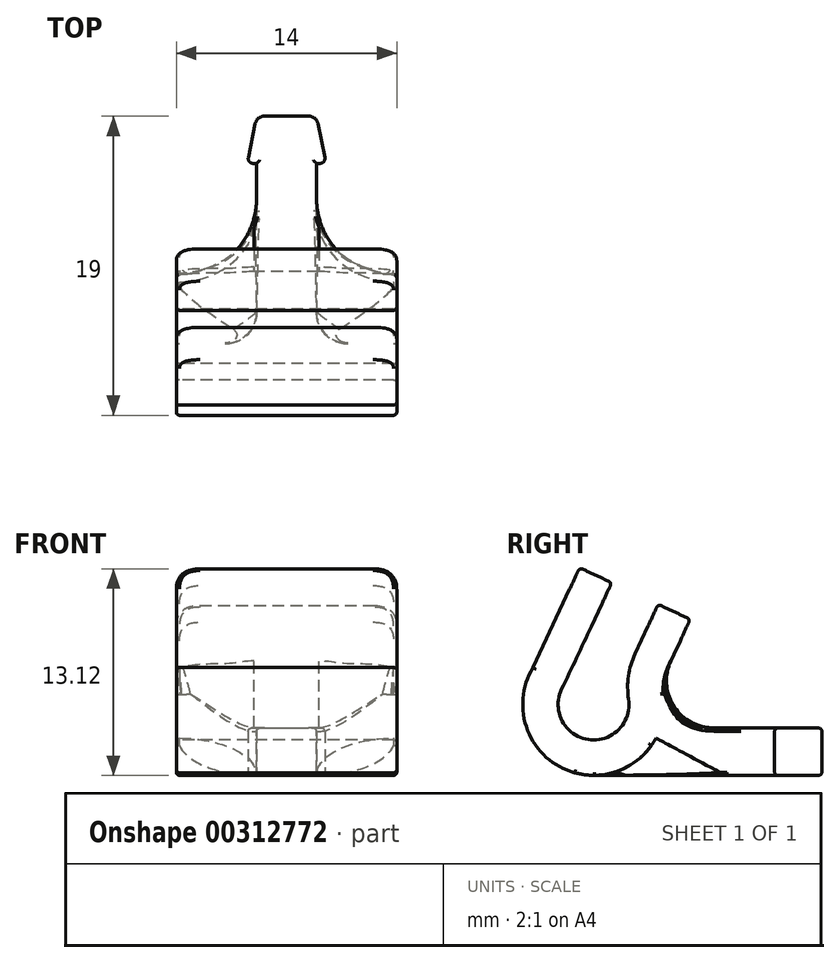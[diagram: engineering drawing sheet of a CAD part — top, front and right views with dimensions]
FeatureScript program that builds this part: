
annotation { "Feature Type Name" : "Feature", "Feature Type Description" : "" }
export const myFeature = defineFeature(function(context is Context, id is Id, definition is map)
    precondition{}
    {
        {
            var Q0;
            Q0=qCreatedBy(makeId("Top.planeOp"),FACE);
            var sketch = newSketch(context, id + "F0", { "sketchPlane" : qUnion([Q0])});
            skLineSegment(sketch, "E0.bottom", {"start": v(-7, -6.95) * mm, "end": v(-3.9, -6.95) * mm});
            skLineSegment(sketch, "E0.top", {"start": v(-7, -8.2) * mm, "end": v(7, -8.2) * mm});
            skLineSegment(sketch, "E0.left", {"start": v(-7, -6.95) * mm, "end": v(-7, -8.2) * mm});
            skLineSegment(sketch, "E0.right", {"start": v(7, -6.95) * mm, "end": v(7, -8.2) * mm});
            skLineSegment(sketch, "E1.bottom", {"start": v(-1.4, 7.5) * mm, "end": v(1.4, 7.5) * mm});
            skLineSegment(sketch, "E1.left", {"start": v(-1.9, 4.5) * mm, "end": v(-1.9, -4.95) * mm});
            skLineSegment(sketch, "E1.right", {"start": v(1.9, 4.5) * mm, "end": v(1.9, -4.95) * mm});
            skLineSegment(sketch, "E2.trimOffspring", {"start": v(3.9, -6.95) * mm, "end": v(7, -6.95) * mm});
            skLineSegment(sketch, "E3", {"start": v(0, 21.87) * mm, "end": v(0, -16.15) * mm, "construction": true});
            skLineSegment(sketch, "E4", {"start": v(-2, 7.02) * mm, "end": v(-2.43, 4.86) * mm});
            skLineSegment(sketch, "E5", {"start": v(-2.13, 4.5) * mm, "end": v(-1.9, 4.5) * mm});
            skLineSegment(sketch, "E6", {"start": v(2.43, 4.86) * mm, "end": v(2, 7.02) * mm});
            skLineSegment(sketch, "E7.trimOffspring", {"start": v(1.9, 4.5) * mm, "end": v(2.13, 4.5) * mm});
            skPoint(sketch, "E8.visualSharp", {"position": v(-1.9, -6.95) * mm});
            skArc(sketch, "E8.filletArc", {"start": v(-3.9, -6.95) * mm, "mid": v(-2.49, -6.36) * mm, "end": v(-1.9, -4.95) * mm});
            skPoint(sketch, "E9.visualSharp", {"position": v(1.9, -6.95) * mm});
            skArc(sketch, "E9.filletArc", {"start": v(1.9, -4.95) * mm, "mid": v(2.49, -6.36) * mm, "end": v(3.9, -6.95) * mm});
            skPoint(sketch, "E10.visualSharp", {"position": v(-1.9, 7.5) * mm});
            skArc(sketch, "E10.filletArc", {"start": v(-1.4, 7.5) * mm, "mid": v(-1.79, 7.36) * mm, "end": v(-2, 7.02) * mm});
            skPoint(sketch, "E11.visualSharp", {"position": v(1.9, 7.5) * mm});
            skArc(sketch, "E11.filletArc", {"start": v(2, 7.02) * mm, "mid": v(1.79, 7.36) * mm, "end": v(1.4, 7.5) * mm});
            skPoint(sketch, "E12.visualSharp", {"position": v(2.5, 4.5) * mm});
            skArc(sketch, "E12.filletArc", {"start": v(2.13, 4.5) * mm, "mid": v(2.37, 4.6) * mm, "end": v(2.43, 4.86) * mm});
            skPoint(sketch, "E13.visualSharp", {"position": v(-2.5, 4.5) * mm});
            skArc(sketch, "E13.filletArc", {"start": v(-2.43, 4.86) * mm, "mid": v(-2.37, 4.6) * mm, "end": v(-2.13, 4.5) * mm});
            skSolve(sketch);
        }
        {
            var Q0;
            Q0 = qSketchRegion(id + "F0", true);
            extrude(context, id + "F1", {"entities" : qUnion([Q0]), "depth" : 3 * mm});
        }
        {
            var Q0;
            Q0=qCreatedBy(makeId("Right.planeOp"),FACE);
            var sketch = newSketch(context, id + "F2", { "sketchPlane" : qUnion([Q0])});
            skArc(sketch, "E14", {"start": v(-10.84, 6.84) * mm, "mid": v(-7.51, 0.03) * mm, "end": v(-2.73, 5.9) * mm});
            skLineSegment(sketch, "E15", {"start": v(-10.84, 6.84) * mm, "end": v(-7.88, 13.19) * mm});
            skLineSegment(sketch, "E16", {"start": v(-7.88, 13.19) * mm, "end": v(-0.86, 9.91) * mm});
            skLineSegment(sketch, "E17", {"start": v(-0.86, 9.91) * mm, "end": v(-2.73, 5.9) * mm});
            skLineSegment(sketch, "E18", {"start": v(-12.4, 0) * mm, "end": v(11.69, 0) * mm, "construction": true});
            skSolve(sketch);
        }
        {
            var Q0;
            Q0 = qSketchRegion(id + "F2", true);
            extrude(context, id + "F3", {"entities" : qUnion([Q0]), "endBound" : BoundingType.SYMMETRIC, "depth" : 14 * mm});
        }
        {
            var Q0;
            Q0=makeQuery(id+"F3.opExtrude","SWEPT_FACE",FACE,{"disambiguationData":[OSD([sQuery(id+"F2.wireOp",EDGE,"E16")])]});
            var Q1;
            Q1=makeQuery(id+"F3.opExtrude","CAP_FACE",FACE,{"disambiguationData":[OSD([sQuery(id+"F2.wireOp",EDGE,"E14"),sQuery(id+"F2.wireOp",EDGE,"E15"),sQuery(id+"F2.wireOp",EDGE,"E16"),sQuery(id+"F2.wireOp",EDGE,"E17")])],"isStart":false});
            var Q2;
            Q2=makeQuery(id+"F3.opExtrude","CAP_FACE",FACE,{"disambiguationData":[OSD([sQuery(id+"F2.wireOp",EDGE,"E14"),sQuery(id+"F2.wireOp",EDGE,"E15"),sQuery(id+"F2.wireOp",EDGE,"E16"),sQuery(id+"F2.wireOp",EDGE,"E17")])],"isStart":true});
            shell(context, id + "F4", {"entities" : qUnion([Q0, Q1, Q2]), "thickness" : 2.25 * mm});
        }
        {
            var Q0;
            Q0=makeQuery(id+"F1.opExtrude","SWEPT_BODY",BODY,{"disambiguationData":[OSD([sQuery(id+"F0.wireOp",EDGE,"E0.bottom"),sQuery(id+"F0.wireOp",EDGE,"E0.top"),sQuery(id+"F0.wireOp",EDGE,"E0.left"),sQuery(id+"F0.wireOp",EDGE,"E0.right"),sQuery(id+"F0.wireOp",EDGE,"E1.bottom"),sQuery(id+"F0.wireOp",EDGE,"E1.left"),sQuery(id+"F0.wireOp",EDGE,"E1.right"),sQuery(id+"F0.wireOp",EDGE,"E2.trimOffspring"),sQuery(id+"F0.wireOp",EDGE,"E4"),sQuery(id+"F0.wireOp",EDGE,"E5"),sQuery(id+"F0.wireOp",EDGE,"E6"),sQuery(id+"F0.wireOp",EDGE,"E7.trimOffspring"),sQuery(id+"F0.wireOp",EDGE,"E8.filletArc"),sQuery(id+"F0.wireOp",EDGE,"E9.filletArc"),sQuery(id+"F0.wireOp",EDGE,"E10.filletArc"),sQuery(id+"F0.wireOp",EDGE,"E11.filletArc"),sQuery(id+"F0.wireOp",EDGE,"E12.filletArc"),sQuery(id+"F0.wireOp",EDGE,"E13.filletArc")])]});
            var Q1;
            Q1=makeQuery(id+"F3.opExtrude","SWEPT_BODY",BODY,{"disambiguationData":[OSD([sQuery(id+"F2.wireOp",EDGE,"E14"),sQuery(id+"F2.wireOp",EDGE,"E15"),sQuery(id+"F2.wireOp",EDGE,"E16"),sQuery(id+"F2.wireOp",EDGE,"E17")])]});
            booleanBodies(context, id + "F5", {"operationType" : BooleanOperationType.UNION, "tools" : qUnion([Q0, Q1])});
        }
        {
            var Q0;
            Q0=makeQuery(id+"F4.opShell","OFFSET_EDGE",EDGE,{"disambiguationData":[OSD([sQuery(id+"F2.wireOp",EDGE,"E14"),sQuery(id+"F2.wireOp",EDGE,"E17")])]});
            fillet(context, id + "F6", {"entities" : qUnion([Q0]), "radius" : 5 * mm, "tangentPropagation" : true, "allowEdgeOverflow" : false});
        }
        {
            var Q0;
            Q0=makeQuery(id+"F5.opBoolean","MERGE",FACE,{"derivedFrom":[makeQuery(id+"F1.opExtrude","SWEPT_FACE",FACE,{"disambiguationData":[OSD([sQuery(id+"F0.wireOp",EDGE,"E0.left")])]}),makeQuery(id+"F3.opExtrude","CAP_FACE",FACE,{"disambiguationData":[OSD([sQuery(id+"F2.wireOp",EDGE,"E14"),sQuery(id+"F2.wireOp",EDGE,"E15"),sQuery(id+"F2.wireOp",EDGE,"E16"),sQuery(id+"F2.wireOp",EDGE,"E17")])],"isStart":true})]});
            var sketch = newSketch(context, id + "F7", { "sketchPlane" : qUnion([Q0])});
            skCircle(sketch, "E19", {"center": v(7, 4.5) * mm, "radius": 2.25 * mm});
            skSolve(sketch);
        }
        {
            var Q0;
            Q0 = qSketchRegion(id + "F7", true);
            extrude(context, id + "F8", {"entities" : qUnion([Q0]), "operationType" : NewBodyOperationType.REMOVE, "endBound" : BoundingType.THROUGH_ALL, "oppositeDirection" : true, "depth" : 14 * mm});
        }
        {
            var Q0;
            Q0=makeQuery(id+"F1.opExtrude","CAP_EDGE",EDGE,{"disambiguationData":[OSD([sQuery(id+"F0.wireOp",EDGE,"E0.top")])],"isStart":true});
            fillet(context, id + "F9", {"entities" : qUnion([Q0]), "radius" : 5 * mm, "tangentPropagation" : true, "allowEdgeOverflow" : false});
        }
        {
            var Q0;
            Q0=makeQuery(id+"F5.opBoolean","INTERSECT",EDGE,{"derivedFrom":[makeQuery(id+"F1.opExtrude","SWEPT_FACE",FACE,{"disambiguationData":[OSD([sQuery(id+"F0.wireOp",EDGE,"E1.right")])]}),makeQuery(id+"F3.opExtrude","SWEPT_FACE",FACE,{"disambiguationData":[OSD([sQuery(id+"F2.wireOp",EDGE,"E14")])]})]});
            var Q1;
            Q1=makeQuery(id+"F5.opBoolean","INTERSECT",EDGE,{"derivedFrom":[makeQuery(id+"F1.opExtrude","SWEPT_FACE",FACE,{"disambiguationData":[OSD([sQuery(id+"F0.wireOp",EDGE,"E9.filletArc")])]}),makeQuery(id+"F3.opExtrude","SWEPT_FACE",FACE,{"disambiguationData":[OSD([sQuery(id+"F2.wireOp",EDGE,"E14")])]})]});
            var Q2;
            {var subQ0=sQuery(id+"F0.wireOp",EDGE,"E1.right");Q2=makeQuery(id+"F11.opFillet","TWEAK_EDGE",EDGE,{"derivedFrom":[makeQuery(id+"F5.opBoolean","INTERSECT",VERTEX,{"derivedFrom":[makeQuery(id+"F1.opExtrude","CAP_FACE",FACE,{"disambiguationData":[OSD([sQuery(id+"F0.wireOp",EDGE,"E0.bottom"),sQuery(id+"F0.wireOp",EDGE,"E0.top"),sQuery(id+"F0.wireOp",EDGE,"E0.left"),sQuery(id+"F0.wireOp",EDGE,"E0.right"),sQuery(id+"F0.wireOp",EDGE,"E1.bottom"),sQuery(id+"F0.wireOp",EDGE,"E1.left"),subQ0,sQuery(id+"F0.wireOp",EDGE,"E2.trimOffspring"),sQuery(id+"F0.wireOp",EDGE,"E4"),sQuery(id+"F0.wireOp",EDGE,"E5"),sQuery(id+"F0.wireOp",EDGE,"E6"),sQuery(id+"F0.wireOp",EDGE,"E7.trimOffspring"),sQuery(id+"F0.wireOp",EDGE,"E8.filletArc"),sQuery(id+"F0.wireOp",EDGE,"E9.filletArc"),sQuery(id+"F0.wireOp",EDGE,"E10.filletArc"),sQuery(id+"F0.wireOp",EDGE,"E11.filletArc"),sQuery(id+"F0.wireOp",EDGE,"E12.filletArc"),sQuery(id+"F0.wireOp",EDGE,"E13.filletArc")])],"isStart":false}),makeQuery(id+"F1.opExtrude","SWEPT_FACE",FACE,{"disambiguationData":[OSD([subQ0])]}),makeQuery(id+"F3.opExtrude","SWEPT_FACE",FACE,{"disambiguationData":[OSD([sQuery(id+"F2.wireOp",EDGE,"E14")])]})]})]});}
            var Q3;
            Q3=makeQuery(id+"F5.opBoolean","INTERSECT",EDGE,{"derivedFrom":[makeQuery(id+"F1.opExtrude","SWEPT_FACE",FACE,{"disambiguationData":[OSD([sQuery(id+"F0.wireOp",EDGE,"E8.filletArc")])]}),makeQuery(id+"F3.opExtrude","SWEPT_FACE",FACE,{"disambiguationData":[OSD([sQuery(id+"F2.wireOp",EDGE,"E14")])]})]});
            var Q4;
            Q4=makeQuery(id+"F5.opBoolean","INTERSECT",EDGE,{"derivedFrom":[makeQuery(id+"F1.opExtrude","SWEPT_FACE",FACE,{"disambiguationData":[OSD([sQuery(id+"F0.wireOp",EDGE,"E1.left")])]}),makeQuery(id+"F3.opExtrude","SWEPT_FACE",FACE,{"disambiguationData":[OSD([sQuery(id+"F2.wireOp",EDGE,"E14")])]})]});
            var Q5;
            {var subQ0=sQuery(id+"F0.wireOp",EDGE,"E1.left");Q5=makeQuery(id+"F11.opFillet","TWEAK_EDGE",EDGE,{"derivedFrom":[makeQuery(id+"F5.opBoolean","INTERSECT",VERTEX,{"derivedFrom":[makeQuery(id+"F1.opExtrude","CAP_FACE",FACE,{"disambiguationData":[OSD([sQuery(id+"F0.wireOp",EDGE,"E0.bottom"),sQuery(id+"F0.wireOp",EDGE,"E0.top"),sQuery(id+"F0.wireOp",EDGE,"E0.left"),sQuery(id+"F0.wireOp",EDGE,"E0.right"),sQuery(id+"F0.wireOp",EDGE,"E1.bottom"),subQ0,sQuery(id+"F0.wireOp",EDGE,"E1.right"),sQuery(id+"F0.wireOp",EDGE,"E2.trimOffspring"),sQuery(id+"F0.wireOp",EDGE,"E4"),sQuery(id+"F0.wireOp",EDGE,"E5"),sQuery(id+"F0.wireOp",EDGE,"E6"),sQuery(id+"F0.wireOp",EDGE,"E7.trimOffspring"),sQuery(id+"F0.wireOp",EDGE,"E8.filletArc"),sQuery(id+"F0.wireOp",EDGE,"E9.filletArc"),sQuery(id+"F0.wireOp",EDGE,"E10.filletArc"),sQuery(id+"F0.wireOp",EDGE,"E11.filletArc"),sQuery(id+"F0.wireOp",EDGE,"E12.filletArc"),sQuery(id+"F0.wireOp",EDGE,"E13.filletArc")])],"isStart":false}),makeQuery(id+"F1.opExtrude","SWEPT_FACE",FACE,{"disambiguationData":[OSD([subQ0])]}),makeQuery(id+"F3.opExtrude","SWEPT_FACE",FACE,{"disambiguationData":[OSD([sQuery(id+"F2.wireOp",EDGE,"E14")])]})]})]});}
            fillet(context, id + "F10", {"entities" : qUnion([Q0, Q1, Q2, Q3, Q4, Q5]), "radius" : 5 * mm, "tangentPropagation" : true, "allowEdgeOverflow" : false});
        }
        {
            var Q0;
            Q0=makeQuery(id+"F5.opBoolean","INTERSECT",EDGE,{"derivedFrom":[makeQuery(id+"F1.opExtrude","CAP_FACE",FACE,{"disambiguationData":[OSD([sQuery(id+"F0.wireOp",EDGE,"E0.bottom"),sQuery(id+"F0.wireOp",EDGE,"E0.top"),sQuery(id+"F0.wireOp",EDGE,"E0.left"),sQuery(id+"F0.wireOp",EDGE,"E0.right"),sQuery(id+"F0.wireOp",EDGE,"E1.bottom"),sQuery(id+"F0.wireOp",EDGE,"E1.left"),sQuery(id+"F0.wireOp",EDGE,"E1.right"),sQuery(id+"F0.wireOp",EDGE,"E2.trimOffspring"),sQuery(id+"F0.wireOp",EDGE,"E4"),sQuery(id+"F0.wireOp",EDGE,"E5"),sQuery(id+"F0.wireOp",EDGE,"E6"),sQuery(id+"F0.wireOp",EDGE,"E7.trimOffspring"),sQuery(id+"F0.wireOp",EDGE,"E8.filletArc"),sQuery(id+"F0.wireOp",EDGE,"E9.filletArc"),sQuery(id+"F0.wireOp",EDGE,"E10.filletArc"),sQuery(id+"F0.wireOp",EDGE,"E11.filletArc"),sQuery(id+"F0.wireOp",EDGE,"E12.filletArc"),sQuery(id+"F0.wireOp",EDGE,"E13.filletArc")])],"isStart":false}),makeQuery(id+"F3.opExtrude","SWEPT_FACE",FACE,{"disambiguationData":[OSD([sQuery(id+"F2.wireOp",EDGE,"E14")])]})]});
            fillet(context, id + "F11", {"entities" : qUnion([Q0]), "radius" : 4 * mm, "tangentPropagation" : true, "rho" : 0.6, "crossSection" : FilletCrossSection.CONIC, "allowEdgeOverflow" : false});
        }
        {
            var Q0;
            Q0=makeQuery(id+"F3.opExtrude","CAP_EDGE",EDGE,{"disambiguationData":[OSD([sQuery(id+"F2.wireOp",EDGE,"E16")])],"isStart":true});
            var Q1;
            {var subQ0=sQuery(id+"F2.wireOp",EDGE,"E16");Q1=makeQuery(id+"F4.opShell","OFFSET_EDGE",EDGE,{"disambiguationData":[OSD([subQ0]),TDD([makeQuery(id+"F3.opExtrude","CAP_EDGE",EDGE,{"disambiguationData":[OSD([subQ0])],"isStart":true})])]});}
            var Q2;
            Q2=makeQuery(id+"F3.opExtrude","CAP_EDGE",EDGE,{"disambiguationData":[OSD([sQuery(id+"F2.wireOp",EDGE,"E16")])],"isStart":false});
            var Q3;
            {var subQ0=sQuery(id+"F2.wireOp",EDGE,"E16");Q3=makeQuery(id+"F4.opShell","OFFSET_EDGE",EDGE,{"disambiguationData":[OSD([subQ0]),TDD([makeQuery(id+"F3.opExtrude","CAP_EDGE",EDGE,{"disambiguationData":[OSD([subQ0])],"isStart":false})])]});}
            fillet(context, id + "F12", {"entities" : qUnion([Q0, Q1, Q2, Q3]), "radius" : 1.5 * mm, "tangentPropagation" : true, "rho" : 0.5, "crossSection" : FilletCrossSection.CONIC, "allowEdgeOverflow" : false});
        }
        {
            var Q0;
            {var subQ0=sQuery(id+"F0.wireOp",EDGE,"E8.filletArc");var subQ1=sQuery(id+"F0.wireOp",EDGE,"E2.trimOffspring");var subQ3=sQuery(id+"F0.wireOp",EDGE,"E1.right");var subQ4=sQuery(id+"F0.wireOp",EDGE,"E1.left");var subQ5=sQuery(id+"F0.wireOp",EDGE,"E0.bottom");var subQ6=sQuery(id+"F0.wireOp",EDGE,"E0.right");var subQ9=sQuery(id+"F2.wireOp",EDGE,"E14");var subQ10=sQuery(id+"F0.wireOp",EDGE,"E9.filletArc");var subQ11=sQuery(id+"F0.wireOp",EDGE,"E0.left");var subQ12=makeQuery(id+"F1.opExtrude","CAP_FACE",FACE,{"disambiguationData":[OSD([subQ5,sQuery(id+"F0.wireOp",EDGE,"E0.top"),subQ11,subQ6,sQuery(id+"F0.wireOp",EDGE,"E1.bottom"),subQ4,subQ3,subQ1,sQuery(id+"F0.wireOp",EDGE,"E4"),sQuery(id+"F0.wireOp",EDGE,"E5"),sQuery(id+"F0.wireOp",EDGE,"E6"),sQuery(id+"F0.wireOp",EDGE,"E7.trimOffspring"),subQ0,subQ10,sQuery(id+"F0.wireOp",EDGE,"E10.filletArc"),sQuery(id+"F0.wireOp",EDGE,"E11.filletArc"),sQuery(id+"F0.wireOp",EDGE,"E12.filletArc"),sQuery(id+"F0.wireOp",EDGE,"E13.filletArc")])],"isStart":false});var subQ13=makeQuery(id+"F3.opExtrude","SWEPT_FACE",FACE,{"disambiguationData":[OSD([subQ9])]});Q0=makeQuery(id+"F11.opFillet","BLEND_EDGE",EDGE,{"blendedFrom":[makeQuery(id+"F5.opBoolean","INTERSECT",EDGE,{"derivedFrom":[subQ12,subQ13]}),makeQuery(id+"F5.opBoolean","SPLIT",FACE,{"disambiguationData":[TD([makeQuery(id+"F1.opExtrude","SWEPT_FACE",FACE,{"disambiguationData":[OSD([subQ5])]})])],"derivedFrom":subQ13})],"blendedInto":[makeQuery(id+"F5.opBoolean","SPLIT",FACE,{"disambiguationData":[TD([makeQuery(id+"F1.opExtrude","SWEPT_FACE",FACE,{"disambiguationData":[OSD([subQ5])]})])],"derivedFrom":subQ13})]});}
            var Q1;
            Q1=makeQuery(id+"F3.opExtrude","SWEPT_EDGE",EDGE,{"disambiguationData":[OSD([sQuery(id+"F2.wireOp",EDGE,"E14"),sQuery(id+"F2.wireOp",EDGE,"E17")])]});
            fillet(context, id + "F13", {"entities" : qUnion([Q0, Q1]), "radius" : 3 * mm, "tangentPropagation" : true, "allowEdgeOverflow" : false});
        }
        {
            var Q0;
            Q0=makeQuery(id+"F1.opExtrude","CAP_EDGE",EDGE,{"disambiguationData":[OSD([sQuery(id+"F0.wireOp",EDGE,"E1.bottom")])],"isStart":true});
            var Q1;
            Q1=makeQuery(id+"F1.opExtrude","CAP_EDGE",EDGE,{"disambiguationData":[OSD([sQuery(id+"F0.wireOp",EDGE,"E11.filletArc")])],"isStart":true});
            var Q2;
            Q2=makeQuery(id+"F1.opExtrude","CAP_EDGE",EDGE,{"disambiguationData":[OSD([sQuery(id+"F0.wireOp",EDGE,"E6")])],"isStart":true});
            var Q3;
            Q3=makeQuery(id+"F1.opExtrude","CAP_EDGE",EDGE,{"disambiguationData":[OSD([sQuery(id+"F0.wireOp",EDGE,"E12.filletArc")])],"isStart":true});
            var Q4;
            Q4=makeQuery(id+"F1.opExtrude","CAP_EDGE",EDGE,{"disambiguationData":[OSD([sQuery(id+"F0.wireOp",EDGE,"E7.trimOffspring")])],"isStart":true});
            var Q5;
            Q5=makeQuery(id+"F1.opExtrude","CAP_EDGE",EDGE,{"disambiguationData":[OSD([sQuery(id+"F0.wireOp",EDGE,"E1.right")])],"isStart":true});
            var Q6;
            Q6=makeQuery(id+"F1.opExtrude","CAP_EDGE",EDGE,{"disambiguationData":[OSD([sQuery(id+"F0.wireOp",EDGE,"E10.filletArc")])],"isStart":true});
            var Q7;
            Q7=makeQuery(id+"F1.opExtrude","CAP_EDGE",EDGE,{"disambiguationData":[OSD([sQuery(id+"F0.wireOp",EDGE,"E4")])],"isStart":true});
            var Q8;
            Q8=makeQuery(id+"F1.opExtrude","CAP_EDGE",EDGE,{"disambiguationData":[OSD([sQuery(id+"F0.wireOp",EDGE,"E13.filletArc")])],"isStart":true});
            var Q9;
            Q9=makeQuery(id+"F1.opExtrude","CAP_EDGE",EDGE,{"disambiguationData":[OSD([sQuery(id+"F0.wireOp",EDGE,"E5")])],"isStart":true});
            var Q10;
            Q10=makeQuery(id+"F1.opExtrude","CAP_EDGE",EDGE,{"disambiguationData":[OSD([sQuery(id+"F0.wireOp",EDGE,"E1.left")])],"isStart":true});
            var Q11;
            {var subQ0=sQuery(id+"F0.wireOp",EDGE,"E1.left");Q11=makeQuery(id+"F10.opFillet","BLEND_EDGE",EDGE,{"blendedFrom":[makeQuery(id+"F5.opBoolean","INTERSECT",EDGE,{"derivedFrom":[makeQuery(id+"F1.opExtrude","SWEPT_FACE",FACE,{"disambiguationData":[OSD([subQ0])]}),makeQuery(id+"F3.opExtrude","SWEPT_FACE",FACE,{"disambiguationData":[OSD([sQuery(id+"F2.wireOp",EDGE,"E14")])]})]}),makeQuery(id+"F1.opExtrude","CAP_FACE",FACE,{"disambiguationData":[OSD([sQuery(id+"F0.wireOp",EDGE,"E0.bottom"),sQuery(id+"F0.wireOp",EDGE,"E0.top"),sQuery(id+"F0.wireOp",EDGE,"E0.left"),sQuery(id+"F0.wireOp",EDGE,"E0.right"),sQuery(id+"F0.wireOp",EDGE,"E1.bottom"),subQ0,sQuery(id+"F0.wireOp",EDGE,"E1.right"),sQuery(id+"F0.wireOp",EDGE,"E2.trimOffspring"),sQuery(id+"F0.wireOp",EDGE,"E4"),sQuery(id+"F0.wireOp",EDGE,"E5"),sQuery(id+"F0.wireOp",EDGE,"E6"),sQuery(id+"F0.wireOp",EDGE,"E7.trimOffspring"),sQuery(id+"F0.wireOp",EDGE,"E8.filletArc"),sQuery(id+"F0.wireOp",EDGE,"E9.filletArc"),sQuery(id+"F0.wireOp",EDGE,"E10.filletArc"),sQuery(id+"F0.wireOp",EDGE,"E11.filletArc"),sQuery(id+"F0.wireOp",EDGE,"E12.filletArc"),sQuery(id+"F0.wireOp",EDGE,"E13.filletArc")])],"isStart":true})],"blendedInto":[makeQuery(id+"F1.opExtrude","CAP_FACE",FACE,{"disambiguationData":[OSD([sQuery(id+"F0.wireOp",EDGE,"E0.bottom"),sQuery(id+"F0.wireOp",EDGE,"E0.top"),sQuery(id+"F0.wireOp",EDGE,"E0.left"),sQuery(id+"F0.wireOp",EDGE,"E0.right"),sQuery(id+"F0.wireOp",EDGE,"E1.bottom"),subQ0,sQuery(id+"F0.wireOp",EDGE,"E1.right"),sQuery(id+"F0.wireOp",EDGE,"E2.trimOffspring"),sQuery(id+"F0.wireOp",EDGE,"E4"),sQuery(id+"F0.wireOp",EDGE,"E5"),sQuery(id+"F0.wireOp",EDGE,"E6"),sQuery(id+"F0.wireOp",EDGE,"E7.trimOffspring"),sQuery(id+"F0.wireOp",EDGE,"E8.filletArc"),sQuery(id+"F0.wireOp",EDGE,"E9.filletArc"),sQuery(id+"F0.wireOp",EDGE,"E10.filletArc"),sQuery(id+"F0.wireOp",EDGE,"E11.filletArc"),sQuery(id+"F0.wireOp",EDGE,"E12.filletArc"),sQuery(id+"F0.wireOp",EDGE,"E13.filletArc")])],"isStart":true})]});}
            var Q12;
            {var subQ0=sQuery(id+"F0.wireOp",EDGE,"E1.right");Q12=makeQuery(id+"F10.opFillet","BLEND_EDGE",EDGE,{"blendedFrom":[makeQuery(id+"F5.opBoolean","INTERSECT",EDGE,{"derivedFrom":[makeQuery(id+"F1.opExtrude","SWEPT_FACE",FACE,{"disambiguationData":[OSD([subQ0])]}),makeQuery(id+"F3.opExtrude","SWEPT_FACE",FACE,{"disambiguationData":[OSD([sQuery(id+"F2.wireOp",EDGE,"E14")])]})]}),makeQuery(id+"F1.opExtrude","CAP_FACE",FACE,{"disambiguationData":[OSD([sQuery(id+"F0.wireOp",EDGE,"E0.bottom"),sQuery(id+"F0.wireOp",EDGE,"E0.top"),sQuery(id+"F0.wireOp",EDGE,"E0.left"),sQuery(id+"F0.wireOp",EDGE,"E0.right"),sQuery(id+"F0.wireOp",EDGE,"E1.bottom"),sQuery(id+"F0.wireOp",EDGE,"E1.left"),subQ0,sQuery(id+"F0.wireOp",EDGE,"E2.trimOffspring"),sQuery(id+"F0.wireOp",EDGE,"E4"),sQuery(id+"F0.wireOp",EDGE,"E5"),sQuery(id+"F0.wireOp",EDGE,"E6"),sQuery(id+"F0.wireOp",EDGE,"E7.trimOffspring"),sQuery(id+"F0.wireOp",EDGE,"E8.filletArc"),sQuery(id+"F0.wireOp",EDGE,"E9.filletArc"),sQuery(id+"F0.wireOp",EDGE,"E10.filletArc"),sQuery(id+"F0.wireOp",EDGE,"E11.filletArc"),sQuery(id+"F0.wireOp",EDGE,"E12.filletArc"),sQuery(id+"F0.wireOp",EDGE,"E13.filletArc")])],"isStart":true})],"blendedInto":[makeQuery(id+"F1.opExtrude","CAP_FACE",FACE,{"disambiguationData":[OSD([sQuery(id+"F0.wireOp",EDGE,"E0.bottom"),sQuery(id+"F0.wireOp",EDGE,"E0.top"),sQuery(id+"F0.wireOp",EDGE,"E0.left"),sQuery(id+"F0.wireOp",EDGE,"E0.right"),sQuery(id+"F0.wireOp",EDGE,"E1.bottom"),sQuery(id+"F0.wireOp",EDGE,"E1.left"),subQ0,sQuery(id+"F0.wireOp",EDGE,"E2.trimOffspring"),sQuery(id+"F0.wireOp",EDGE,"E4"),sQuery(id+"F0.wireOp",EDGE,"E5"),sQuery(id+"F0.wireOp",EDGE,"E6"),sQuery(id+"F0.wireOp",EDGE,"E7.trimOffspring"),sQuery(id+"F0.wireOp",EDGE,"E8.filletArc"),sQuery(id+"F0.wireOp",EDGE,"E9.filletArc"),sQuery(id+"F0.wireOp",EDGE,"E10.filletArc"),sQuery(id+"F0.wireOp",EDGE,"E11.filletArc"),sQuery(id+"F0.wireOp",EDGE,"E12.filletArc"),sQuery(id+"F0.wireOp",EDGE,"E13.filletArc")])],"isStart":true})]});}
            fillet(context, id + "F14", {"entities" : qUnion([Q0, Q1, Q2, Q3, Q4, Q5, Q6, Q7, Q8, Q9, Q10, Q11, Q12]), "radius" : 0.2 * mm, "tangentPropagation" : true, "allowEdgeOverflow" : false});
        }
        {
            var Q0;
            {var subQ0=sQuery(id+"F2.wireOp",EDGE,"E14");var subQ1=sQuery(id+"F0.wireOp",EDGE,"E1.left");Q0=makeQuery(id+"F11.opFillet","BLEND_EDGE",EDGE,{"blendedFrom":[makeQuery(id+"F5.opBoolean","INTERSECT",EDGE,{"derivedFrom":[makeQuery(id+"F1.opExtrude","CAP_FACE",FACE,{"disambiguationData":[OSD([sQuery(id+"F0.wireOp",EDGE,"E0.bottom"),sQuery(id+"F0.wireOp",EDGE,"E0.top"),sQuery(id+"F0.wireOp",EDGE,"E0.left"),sQuery(id+"F0.wireOp",EDGE,"E0.right"),sQuery(id+"F0.wireOp",EDGE,"E1.bottom"),subQ1,sQuery(id+"F0.wireOp",EDGE,"E1.right"),sQuery(id+"F0.wireOp",EDGE,"E2.trimOffspring"),sQuery(id+"F0.wireOp",EDGE,"E4"),sQuery(id+"F0.wireOp",EDGE,"E5"),sQuery(id+"F0.wireOp",EDGE,"E6"),sQuery(id+"F0.wireOp",EDGE,"E7.trimOffspring"),sQuery(id+"F0.wireOp",EDGE,"E8.filletArc"),sQuery(id+"F0.wireOp",EDGE,"E9.filletArc"),sQuery(id+"F0.wireOp",EDGE,"E10.filletArc"),sQuery(id+"F0.wireOp",EDGE,"E11.filletArc"),sQuery(id+"F0.wireOp",EDGE,"E12.filletArc"),sQuery(id+"F0.wireOp",EDGE,"E13.filletArc")])],"isStart":false}),makeQuery(id+"F3.opExtrude","SWEPT_FACE",FACE,{"disambiguationData":[OSD([subQ0])]})]}),makeQuery(id+"F10.opFillet","BLEND_FACE",FACE,{"disambiguationData":[OSD([subQ1,subQ0])]})],"blendedInto":[makeQuery(id+"F10.opFillet","BLEND_FACE",FACE,{"disambiguationData":[OSD([subQ1,subQ0])]})]});}
            var Q1;
            Q1=makeQuery(id+"F1.opExtrude","CAP_EDGE",EDGE,{"disambiguationData":[OSD([sQuery(id+"F0.wireOp",EDGE,"E1.left")])],"isStart":false});
            var Q2;
            {var subQ0=sQuery(id+"F0.wireOp",EDGE,"E10.filletArc");var subQ1=sQuery(id+"F0.wireOp",EDGE,"E7.trimOffspring");var subQ2=sQuery(id+"F0.wireOp",EDGE,"E6");var subQ3=sQuery(id+"F0.wireOp",EDGE,"E5");var subQ4=sQuery(id+"F0.wireOp",EDGE,"E11.filletArc");var subQ5=sQuery(id+"F0.wireOp",EDGE,"E1.bottom");var subQ6=sQuery(id+"F0.wireOp",EDGE,"E12.filletArc");var subQ7=sQuery(id+"F0.wireOp",EDGE,"E1.left");var subQ8=makeQuery(id+"F1.opExtrude","SWEPT_FACE",FACE,{"disambiguationData":[OSD([subQ7])]});var subQ9=sQuery(id+"F0.wireOp",EDGE,"E1.right");var subQ10=sQuery(id+"F0.wireOp",EDGE,"E4");var subQ11=sQuery(id+"F0.wireOp",EDGE,"E13.filletArc");var subQ12=makeQuery(id+"F3.opExtrude","SWEPT_FACE",FACE,{"disambiguationData":[OSD([sQuery(id+"F2.wireOp",EDGE,"E14")])]});Q2=makeQuery(id+"F10.opFillet","BLEND_EDGE",EDGE,{"blendedFrom":[makeQuery(id+"F5.opBoolean","INTERSECT",EDGE,{"derivedFrom":[subQ8,subQ12]}),makeQuery(id+"F5.opBoolean","SPLIT",FACE,{"disambiguationData":[TD([makeQuery(id+"F1.opExtrude","SWEPT_FACE",FACE,{"disambiguationData":[OSD([subQ5])]})])],"derivedFrom":makeQuery(id+"F1.opExtrude","CAP_FACE",FACE,{"disambiguationData":[OSD([sQuery(id+"F0.wireOp",EDGE,"E0.bottom"),sQuery(id+"F0.wireOp",EDGE,"E0.top"),sQuery(id+"F0.wireOp",EDGE,"E0.left"),sQuery(id+"F0.wireOp",EDGE,"E0.right"),subQ5,subQ7,subQ9,sQuery(id+"F0.wireOp",EDGE,"E2.trimOffspring"),subQ10,subQ3,subQ2,subQ1,sQuery(id+"F0.wireOp",EDGE,"E8.filletArc"),sQuery(id+"F0.wireOp",EDGE,"E9.filletArc"),subQ0,subQ4,subQ6,subQ11])],"isStart":false})})],"blendedInto":[makeQuery(id+"F5.opBoolean","SPLIT",FACE,{"disambiguationData":[TD([makeQuery(id+"F1.opExtrude","SWEPT_FACE",FACE,{"disambiguationData":[OSD([subQ5])]})])],"derivedFrom":makeQuery(id+"F1.opExtrude","CAP_FACE",FACE,{"disambiguationData":[OSD([sQuery(id+"F0.wireOp",EDGE,"E0.bottom"),sQuery(id+"F0.wireOp",EDGE,"E0.top"),sQuery(id+"F0.wireOp",EDGE,"E0.left"),sQuery(id+"F0.wireOp",EDGE,"E0.right"),subQ5,subQ7,subQ9,sQuery(id+"F0.wireOp",EDGE,"E2.trimOffspring"),subQ10,subQ3,subQ2,subQ1,sQuery(id+"F0.wireOp",EDGE,"E8.filletArc"),sQuery(id+"F0.wireOp",EDGE,"E9.filletArc"),subQ0,subQ4,subQ6,subQ11])],"isStart":false})})]});}
            var Q3;
            Q3=makeQuery(id+"F1.opExtrude","CAP_EDGE",EDGE,{"disambiguationData":[OSD([sQuery(id+"F0.wireOp",EDGE,"E5")])],"isStart":false});
            var Q4;
            Q4=makeQuery(id+"F1.opExtrude","CAP_EDGE",EDGE,{"disambiguationData":[OSD([sQuery(id+"F0.wireOp",EDGE,"E13.filletArc")])],"isStart":false});
            var Q5;
            Q5=makeQuery(id+"F1.opExtrude","CAP_EDGE",EDGE,{"disambiguationData":[OSD([sQuery(id+"F0.wireOp",EDGE,"E4")])],"isStart":false});
            var Q6;
            Q6=makeQuery(id+"F1.opExtrude","CAP_EDGE",EDGE,{"disambiguationData":[OSD([sQuery(id+"F0.wireOp",EDGE,"E10.filletArc")])],"isStart":false});
            var Q7;
            Q7=makeQuery(id+"F1.opExtrude","CAP_EDGE",EDGE,{"disambiguationData":[OSD([sQuery(id+"F0.wireOp",EDGE,"E1.bottom")])],"isStart":false});
            var Q8;
            Q8=makeQuery(id+"F1.opExtrude","CAP_EDGE",EDGE,{"disambiguationData":[OSD([sQuery(id+"F0.wireOp",EDGE,"E11.filletArc")])],"isStart":false});
            var Q9;
            Q9=makeQuery(id+"F1.opExtrude","CAP_EDGE",EDGE,{"disambiguationData":[OSD([sQuery(id+"F0.wireOp",EDGE,"E6")])],"isStart":false});
            var Q10;
            Q10=makeQuery(id+"F1.opExtrude","CAP_EDGE",EDGE,{"disambiguationData":[OSD([sQuery(id+"F0.wireOp",EDGE,"E12.filletArc")])],"isStart":false});
            var Q11;
            Q11=makeQuery(id+"F1.opExtrude","CAP_EDGE",EDGE,{"disambiguationData":[OSD([sQuery(id+"F0.wireOp",EDGE,"E1.right")])],"isStart":false});
            var Q12;
            Q12=makeQuery(id+"F1.opExtrude","CAP_EDGE",EDGE,{"disambiguationData":[OSD([sQuery(id+"F0.wireOp",EDGE,"E7.trimOffspring")])],"isStart":false});
            var Q13;
            {var subQ0=sQuery(id+"F0.wireOp",EDGE,"E10.filletArc");var subQ1=sQuery(id+"F0.wireOp",EDGE,"E7.trimOffspring");var subQ2=sQuery(id+"F0.wireOp",EDGE,"E6");var subQ3=sQuery(id+"F0.wireOp",EDGE,"E5");var subQ4=sQuery(id+"F0.wireOp",EDGE,"E11.filletArc");var subQ5=sQuery(id+"F0.wireOp",EDGE,"E1.bottom");var subQ6=sQuery(id+"F0.wireOp",EDGE,"E12.filletArc");var subQ7=sQuery(id+"F0.wireOp",EDGE,"E1.left");var subQ8=sQuery(id+"F0.wireOp",EDGE,"E1.right");var subQ9=makeQuery(id+"F1.opExtrude","SWEPT_FACE",FACE,{"disambiguationData":[OSD([subQ8])]});var subQ10=sQuery(id+"F0.wireOp",EDGE,"E4");var subQ11=sQuery(id+"F0.wireOp",EDGE,"E13.filletArc");var subQ12=makeQuery(id+"F3.opExtrude","SWEPT_FACE",FACE,{"disambiguationData":[OSD([sQuery(id+"F2.wireOp",EDGE,"E14")])]});Q13=makeQuery(id+"F10.opFillet","BLEND_EDGE",EDGE,{"blendedFrom":[makeQuery(id+"F5.opBoolean","INTERSECT",EDGE,{"derivedFrom":[subQ9,subQ12]}),makeQuery(id+"F5.opBoolean","SPLIT",FACE,{"disambiguationData":[TD([makeQuery(id+"F1.opExtrude","SWEPT_FACE",FACE,{"disambiguationData":[OSD([subQ5])]})])],"derivedFrom":makeQuery(id+"F1.opExtrude","CAP_FACE",FACE,{"disambiguationData":[OSD([sQuery(id+"F0.wireOp",EDGE,"E0.bottom"),sQuery(id+"F0.wireOp",EDGE,"E0.top"),sQuery(id+"F0.wireOp",EDGE,"E0.left"),sQuery(id+"F0.wireOp",EDGE,"E0.right"),subQ5,subQ7,subQ8,sQuery(id+"F0.wireOp",EDGE,"E2.trimOffspring"),subQ10,subQ3,subQ2,subQ1,sQuery(id+"F0.wireOp",EDGE,"E8.filletArc"),sQuery(id+"F0.wireOp",EDGE,"E9.filletArc"),subQ0,subQ4,subQ6,subQ11])],"isStart":false})})],"blendedInto":[makeQuery(id+"F5.opBoolean","SPLIT",FACE,{"disambiguationData":[TD([makeQuery(id+"F1.opExtrude","SWEPT_FACE",FACE,{"disambiguationData":[OSD([subQ5])]})])],"derivedFrom":makeQuery(id+"F1.opExtrude","CAP_FACE",FACE,{"disambiguationData":[OSD([sQuery(id+"F0.wireOp",EDGE,"E0.bottom"),sQuery(id+"F0.wireOp",EDGE,"E0.top"),sQuery(id+"F0.wireOp",EDGE,"E0.left"),sQuery(id+"F0.wireOp",EDGE,"E0.right"),subQ5,subQ7,subQ8,sQuery(id+"F0.wireOp",EDGE,"E2.trimOffspring"),subQ10,subQ3,subQ2,subQ1,sQuery(id+"F0.wireOp",EDGE,"E8.filletArc"),sQuery(id+"F0.wireOp",EDGE,"E9.filletArc"),subQ0,subQ4,subQ6,subQ11])],"isStart":false})})]});}
            var Q14;
            {var subQ0=sQuery(id+"F2.wireOp",EDGE,"E14");var subQ1=sQuery(id+"F0.wireOp",EDGE,"E1.right");Q14=makeQuery(id+"F11.opFillet","BLEND_EDGE",EDGE,{"blendedFrom":[makeQuery(id+"F5.opBoolean","INTERSECT",EDGE,{"derivedFrom":[makeQuery(id+"F1.opExtrude","CAP_FACE",FACE,{"disambiguationData":[OSD([sQuery(id+"F0.wireOp",EDGE,"E0.bottom"),sQuery(id+"F0.wireOp",EDGE,"E0.top"),sQuery(id+"F0.wireOp",EDGE,"E0.left"),sQuery(id+"F0.wireOp",EDGE,"E0.right"),sQuery(id+"F0.wireOp",EDGE,"E1.bottom"),sQuery(id+"F0.wireOp",EDGE,"E1.left"),subQ1,sQuery(id+"F0.wireOp",EDGE,"E2.trimOffspring"),sQuery(id+"F0.wireOp",EDGE,"E4"),sQuery(id+"F0.wireOp",EDGE,"E5"),sQuery(id+"F0.wireOp",EDGE,"E6"),sQuery(id+"F0.wireOp",EDGE,"E7.trimOffspring"),sQuery(id+"F0.wireOp",EDGE,"E8.filletArc"),sQuery(id+"F0.wireOp",EDGE,"E9.filletArc"),sQuery(id+"F0.wireOp",EDGE,"E10.filletArc"),sQuery(id+"F0.wireOp",EDGE,"E11.filletArc"),sQuery(id+"F0.wireOp",EDGE,"E12.filletArc"),sQuery(id+"F0.wireOp",EDGE,"E13.filletArc")])],"isStart":false}),makeQuery(id+"F3.opExtrude","SWEPT_FACE",FACE,{"disambiguationData":[OSD([subQ0])]})]}),makeQuery(id+"F10.opFillet","BLEND_FACE",FACE,{"disambiguationData":[OSD([subQ1,subQ0])]})],"blendedInto":[makeQuery(id+"F10.opFillet","BLEND_FACE",FACE,{"disambiguationData":[OSD([subQ1,subQ0])]})]});}
            fillet(context, id + "F15", {"entities" : qUnion([Q0, Q1, Q2, Q3, Q4, Q5, Q6, Q7, Q8, Q9, Q10, Q11, Q12, Q13, Q14]), "radius" : 0.2 * mm, "tangentPropagation" : true, "allowEdgeOverflow" : false});
        }
        {
            var Q0;
            Q0=makeQuery(id+"F3.opExtrude","SWEPT_EDGE",EDGE,{"disambiguationData":[OSD([sQuery(id+"F2.wireOp",EDGE,"E16"),sQuery(id+"F2.wireOp",EDGE,"E17")])]});
            var Q1;
            {var subQ0=sQuery(id+"F2.wireOp",EDGE,"E16");Q1=makeQuery(id+"F12.opFillet","BLEND_EDGE",EDGE,{"blendedFrom":[makeQuery(id+"F4.opShell","OFFSET_EDGE",EDGE,{"disambiguationData":[OSD([subQ0]),TDD([makeQuery(id+"F3.opExtrude","CAP_EDGE",EDGE,{"disambiguationData":[OSD([subQ0])],"isStart":false})])]}),makeQuery(id+"F3.opExtrude","SWEPT_FACE",FACE,{"disambiguationData":[OSD([sQuery(id+"F2.wireOp",EDGE,"E17")])]})],"blendedInto":[makeQuery(id+"F3.opExtrude","SWEPT_FACE",FACE,{"disambiguationData":[OSD([sQuery(id+"F2.wireOp",EDGE,"E17")])]})]});}
            var Q2;
            Q2=makeQuery(id+"F3.opExtrude","CAP_EDGE",EDGE,{"disambiguationData":[OSD([sQuery(id+"F2.wireOp",EDGE,"E17")])],"isStart":false});
            var Q3;
            {var subQ0=sQuery(id+"F2.wireOp",EDGE,"E17");var subQ1=sQuery(id+"F2.wireOp",EDGE,"E14");Q3=makeQuery(id+"F13.opFillet","BLEND_EDGE",EDGE,{"blendedFrom":[makeQuery(id+"F3.opExtrude","SWEPT_EDGE",EDGE,{"disambiguationData":[OSD([subQ1,subQ0])]}),makeQuery(id+"F5.opBoolean","MERGE",FACE,{"derivedFrom":[makeQuery(id+"F1.opExtrude","SWEPT_FACE",FACE,{"disambiguationData":[OSD([sQuery(id+"F0.wireOp",EDGE,"E0.right")])]}),makeQuery(id+"F3.opExtrude","CAP_FACE",FACE,{"disambiguationData":[OSD([subQ1,sQuery(id+"F2.wireOp",EDGE,"E15"),sQuery(id+"F2.wireOp",EDGE,"E16"),subQ0])],"isStart":false})]})],"blendedInto":[makeQuery(id+"F5.opBoolean","MERGE",FACE,{"derivedFrom":[makeQuery(id+"F1.opExtrude","SWEPT_FACE",FACE,{"disambiguationData":[OSD([sQuery(id+"F0.wireOp",EDGE,"E0.right")])]}),makeQuery(id+"F3.opExtrude","CAP_FACE",FACE,{"disambiguationData":[OSD([subQ1,sQuery(id+"F2.wireOp",EDGE,"E15"),sQuery(id+"F2.wireOp",EDGE,"E16"),subQ0])],"isStart":false})]})]});}
            var Q4;
            {var subQ0=sQuery(id+"F2.wireOp",EDGE,"E14");Q4=makeQuery(id+"F5.opBoolean","SPLIT",EDGE,{"disambiguationData":[TD([makeQuery(id+"F1.opExtrude","SWEPT_FACE",FACE,{"disambiguationData":[OSD([sQuery(id+"F0.wireOp",EDGE,"E2.trimOffspring")])]})])],"derivedFrom":makeQuery(id+"F3.opExtrude","CAP_EDGE",EDGE,{"disambiguationData":[OSD([subQ0])],"isStart":false})});}
            var Q5;
            {var subQ0=sQuery(id+"F2.wireOp",EDGE,"E16");Q5=makeQuery(id+"F12.opFillet","BLEND_EDGE",EDGE,{"blendedFrom":[makeQuery(id+"F4.opShell","OFFSET_EDGE",EDGE,{"disambiguationData":[OSD([subQ0]),TDD([makeQuery(id+"F3.opExtrude","CAP_EDGE",EDGE,{"disambiguationData":[OSD([subQ0])],"isStart":true})])]}),makeQuery(id+"F3.opExtrude","SWEPT_FACE",FACE,{"disambiguationData":[OSD([sQuery(id+"F2.wireOp",EDGE,"E17")])]})],"blendedInto":[makeQuery(id+"F3.opExtrude","SWEPT_FACE",FACE,{"disambiguationData":[OSD([sQuery(id+"F2.wireOp",EDGE,"E17")])]})]});}
            var Q6;
            Q6=makeQuery(id+"F3.opExtrude","CAP_EDGE",EDGE,{"disambiguationData":[OSD([sQuery(id+"F2.wireOp",EDGE,"E17")])],"isStart":true});
            var Q7;
            Q7=makeQuery(id+"F9.opFillet","BLEND_EDGE",EDGE,{"blendedFrom":[makeQuery(id+"F1.opExtrude","CAP_EDGE",EDGE,{"disambiguationData":[OSD([sQuery(id+"F0.wireOp",EDGE,"E0.top")])],"isStart":true}),makeQuery(id+"F5.opBoolean","MERGE",FACE,{"derivedFrom":[makeQuery(id+"F1.opExtrude","SWEPT_FACE",FACE,{"disambiguationData":[OSD([sQuery(id+"F0.wireOp",EDGE,"E0.right")])]}),makeQuery(id+"F3.opExtrude","CAP_FACE",FACE,{"disambiguationData":[OSD([sQuery(id+"F2.wireOp",EDGE,"E14"),sQuery(id+"F2.wireOp",EDGE,"E15"),sQuery(id+"F2.wireOp",EDGE,"E16"),sQuery(id+"F2.wireOp",EDGE,"E17")])],"isStart":false})]})],"blendedInto":[makeQuery(id+"F5.opBoolean","MERGE",FACE,{"derivedFrom":[makeQuery(id+"F1.opExtrude","SWEPT_FACE",FACE,{"disambiguationData":[OSD([sQuery(id+"F0.wireOp",EDGE,"E0.right")])]}),makeQuery(id+"F3.opExtrude","CAP_FACE",FACE,{"disambiguationData":[OSD([sQuery(id+"F2.wireOp",EDGE,"E14"),sQuery(id+"F2.wireOp",EDGE,"E15"),sQuery(id+"F2.wireOp",EDGE,"E16"),sQuery(id+"F2.wireOp",EDGE,"E17")])],"isStart":false})]})]});
            var Q8;
            {var subQ1=sQuery(id+"F2.wireOp",EDGE,"E14");Q8=makeQuery(id+"F5.opBoolean","SPLIT",EDGE,{"disambiguationData":[TD([makeQuery(id+"F1.opExtrude","SWEPT_FACE",FACE,{"disambiguationData":[OSD([sQuery(id+"F0.wireOp",EDGE,"E0.top")])]})])],"derivedFrom":makeQuery(id+"F3.opExtrude","CAP_EDGE",EDGE,{"disambiguationData":[OSD([subQ1])],"isStart":false})});}
            var Q9;
            Q9=makeQuery(id+"F3.opExtrude","CAP_EDGE",EDGE,{"disambiguationData":[OSD([sQuery(id+"F2.wireOp",EDGE,"E15")])],"isStart":false});
            var Q10;
            Q10=makeQuery(id+"F12.opFillet","BLEND_EDGE",EDGE,{"blendedFrom":[makeQuery(id+"F3.opExtrude","CAP_EDGE",EDGE,{"disambiguationData":[OSD([sQuery(id+"F2.wireOp",EDGE,"E16")])],"isStart":false}),makeQuery(id+"F3.opExtrude","SWEPT_FACE",FACE,{"disambiguationData":[OSD([sQuery(id+"F2.wireOp",EDGE,"E15")])]})],"blendedInto":[makeQuery(id+"F3.opExtrude","SWEPT_FACE",FACE,{"disambiguationData":[OSD([sQuery(id+"F2.wireOp",EDGE,"E15")])]})]});
            var Q11;
            Q11=makeQuery(id+"F3.opExtrude","SWEPT_EDGE",EDGE,{"disambiguationData":[OSD([sQuery(id+"F2.wireOp",EDGE,"E15"),sQuery(id+"F2.wireOp",EDGE,"E16")])]});
            var Q12;
            Q12=makeQuery(id+"F12.opFillet","BLEND_EDGE",EDGE,{"blendedFrom":[makeQuery(id+"F3.opExtrude","CAP_EDGE",EDGE,{"disambiguationData":[OSD([sQuery(id+"F2.wireOp",EDGE,"E16")])],"isStart":true}),makeQuery(id+"F3.opExtrude","SWEPT_FACE",FACE,{"disambiguationData":[OSD([sQuery(id+"F2.wireOp",EDGE,"E15")])]})],"blendedInto":[makeQuery(id+"F3.opExtrude","SWEPT_FACE",FACE,{"disambiguationData":[OSD([sQuery(id+"F2.wireOp",EDGE,"E15")])]})]});
            var Q13;
            Q13=makeQuery(id+"F3.opExtrude","CAP_EDGE",EDGE,{"disambiguationData":[OSD([sQuery(id+"F2.wireOp",EDGE,"E15")])],"isStart":true});
            var Q14;
            {var subQ1=sQuery(id+"F2.wireOp",EDGE,"E14");Q14=makeQuery(id+"F5.opBoolean","SPLIT",EDGE,{"disambiguationData":[TD([makeQuery(id+"F1.opExtrude","SWEPT_FACE",FACE,{"disambiguationData":[OSD([sQuery(id+"F0.wireOp",EDGE,"E0.top")])]})])],"derivedFrom":makeQuery(id+"F3.opExtrude","CAP_EDGE",EDGE,{"disambiguationData":[OSD([subQ1])],"isStart":true})});}
            var Q15;
            Q15=makeQuery(id+"F9.opFillet","BLEND_EDGE",EDGE,{"blendedFrom":[makeQuery(id+"F1.opExtrude","CAP_EDGE",EDGE,{"disambiguationData":[OSD([sQuery(id+"F0.wireOp",EDGE,"E0.top")])],"isStart":true}),makeQuery(id+"F5.opBoolean","MERGE",FACE,{"derivedFrom":[makeQuery(id+"F1.opExtrude","SWEPT_FACE",FACE,{"disambiguationData":[OSD([sQuery(id+"F0.wireOp",EDGE,"E0.left")])]}),makeQuery(id+"F3.opExtrude","CAP_FACE",FACE,{"disambiguationData":[OSD([sQuery(id+"F2.wireOp",EDGE,"E14"),sQuery(id+"F2.wireOp",EDGE,"E15"),sQuery(id+"F2.wireOp",EDGE,"E16"),sQuery(id+"F2.wireOp",EDGE,"E17")])],"isStart":true})]})],"blendedInto":[makeQuery(id+"F5.opBoolean","MERGE",FACE,{"derivedFrom":[makeQuery(id+"F1.opExtrude","SWEPT_FACE",FACE,{"disambiguationData":[OSD([sQuery(id+"F0.wireOp",EDGE,"E0.left")])]}),makeQuery(id+"F3.opExtrude","CAP_FACE",FACE,{"disambiguationData":[OSD([sQuery(id+"F2.wireOp",EDGE,"E14"),sQuery(id+"F2.wireOp",EDGE,"E15"),sQuery(id+"F2.wireOp",EDGE,"E16"),sQuery(id+"F2.wireOp",EDGE,"E17")])],"isStart":true})]})]});
            var Q16;
            {var subQ0=sQuery(id+"F2.wireOp",EDGE,"E14");Q16=makeQuery(id+"F5.opBoolean","SPLIT",EDGE,{"disambiguationData":[TD([makeQuery(id+"F1.opExtrude","SWEPT_FACE",FACE,{"disambiguationData":[OSD([sQuery(id+"F0.wireOp",EDGE,"E0.bottom")])]})])],"derivedFrom":makeQuery(id+"F3.opExtrude","CAP_EDGE",EDGE,{"disambiguationData":[OSD([subQ0])],"isStart":true})});}
            var Q17;
            {var subQ0=sQuery(id+"F2.wireOp",EDGE,"E17");var subQ1=sQuery(id+"F2.wireOp",EDGE,"E14");Q17=makeQuery(id+"F13.opFillet","BLEND_EDGE",EDGE,{"blendedFrom":[makeQuery(id+"F3.opExtrude","SWEPT_EDGE",EDGE,{"disambiguationData":[OSD([subQ1,subQ0])]}),makeQuery(id+"F5.opBoolean","MERGE",FACE,{"derivedFrom":[makeQuery(id+"F1.opExtrude","SWEPT_FACE",FACE,{"disambiguationData":[OSD([sQuery(id+"F0.wireOp",EDGE,"E0.left")])]}),makeQuery(id+"F3.opExtrude","CAP_FACE",FACE,{"disambiguationData":[OSD([subQ1,sQuery(id+"F2.wireOp",EDGE,"E15"),sQuery(id+"F2.wireOp",EDGE,"E16"),subQ0])],"isStart":true})]})],"blendedInto":[makeQuery(id+"F5.opBoolean","MERGE",FACE,{"derivedFrom":[makeQuery(id+"F1.opExtrude","SWEPT_FACE",FACE,{"disambiguationData":[OSD([sQuery(id+"F0.wireOp",EDGE,"E0.left")])]}),makeQuery(id+"F3.opExtrude","CAP_FACE",FACE,{"disambiguationData":[OSD([subQ1,sQuery(id+"F2.wireOp",EDGE,"E15"),sQuery(id+"F2.wireOp",EDGE,"E16"),subQ0])],"isStart":true})]})]});}
            fillet(context, id + "F16", {"entities" : qUnion([Q0, Q1, Q2, Q3, Q4, Q5, Q6, Q7, Q8, Q9, Q10, Q11, Q12, Q13, Q14, Q15, Q16, Q17]), "radius" : 0.2 * mm, "tangentPropagation" : true, "allowEdgeOverflow" : false});
        }
        {
            var Q0;
            {var subQ0=sQuery(id+"F2.wireOp",EDGE,"E14");var subQ6=makeQuery(id+"F4.opShell","OFFSET_EDGE",EDGE,{"disambiguationData":[OSD([subQ0]),TDD([makeQuery(id+"F3.opExtrude","CAP_EDGE",EDGE,{"disambiguationData":[OSD([subQ0])],"isStart":true})])]});Q0=makeQuery(id+"F8.boolean.opBoolean","MERGE",EDGE,{"derivedFrom":[makeQuery(id+"F5.opBoolean","SPLIT",EDGE,{"disambiguationData":[TD([makeQuery(id+"F1.opExtrude","SWEPT_FACE",FACE,{"disambiguationData":[OSD([sQuery(id+"F0.wireOp",EDGE,"E0.top")])]})])],"derivedFrom":subQ6}),makeQuery(id+"F5.opBoolean","SPLIT",EDGE,{"disambiguationData":[TD([makeQuery(id+"F1.opExtrude","SWEPT_FACE",FACE,{"disambiguationData":[OSD([sQuery(id+"F0.wireOp",EDGE,"E0.bottom")])]})])],"derivedFrom":subQ6}),makeQuery(id+"F8.opExtrude","CAP_EDGE",EDGE,{"disambiguationData":[OSD([sQuery(id+"F7.wireOp",EDGE,"E19")])],"isStart":true})]});}
            var Q1;
            {var subQ0=sQuery(id+"F2.wireOp",EDGE,"E17");var subQ1=sQuery(id+"F2.wireOp",EDGE,"E14");Q1=makeQuery(id+"F6.opFillet","BLEND_EDGE",EDGE,{"blendedFrom":[makeQuery(id+"F4.opShell","OFFSET_EDGE",EDGE,{"disambiguationData":[OSD([subQ1,subQ0])]}),makeQuery(id+"F5.opBoolean","MERGE",FACE,{"derivedFrom":[makeQuery(id+"F1.opExtrude","SWEPT_FACE",FACE,{"disambiguationData":[OSD([sQuery(id+"F0.wireOp",EDGE,"E0.left")])]}),makeQuery(id+"F3.opExtrude","CAP_FACE",FACE,{"disambiguationData":[OSD([subQ1,sQuery(id+"F2.wireOp",EDGE,"E15"),sQuery(id+"F2.wireOp",EDGE,"E16"),subQ0])],"isStart":true})]})],"blendedInto":[makeQuery(id+"F5.opBoolean","MERGE",FACE,{"derivedFrom":[makeQuery(id+"F1.opExtrude","SWEPT_FACE",FACE,{"disambiguationData":[OSD([sQuery(id+"F0.wireOp",EDGE,"E0.left")])]}),makeQuery(id+"F3.opExtrude","CAP_FACE",FACE,{"disambiguationData":[OSD([subQ1,sQuery(id+"F2.wireOp",EDGE,"E15"),sQuery(id+"F2.wireOp",EDGE,"E16"),subQ0])],"isStart":true})]})]});}
            var Q2;
            {var subQ0=sQuery(id+"F2.wireOp",EDGE,"E17");Q2=makeQuery(id+"F4.opShell","OFFSET_EDGE",EDGE,{"disambiguationData":[OSD([subQ0]),TDD([makeQuery(id+"F3.opExtrude","CAP_EDGE",EDGE,{"disambiguationData":[OSD([subQ0])],"isStart":true})])]});}
            var Q3;
            {var subQ0=sQuery(id+"F2.wireOp",EDGE,"E16");Q3=makeQuery(id+"F12.opFillet","BLEND_EDGE",EDGE,{"blendedFrom":[makeQuery(id+"F4.opShell","OFFSET_EDGE",EDGE,{"disambiguationData":[OSD([subQ0]),TDD([makeQuery(id+"F3.opExtrude","CAP_EDGE",EDGE,{"disambiguationData":[OSD([subQ0])],"isStart":true})])]}),makeQuery(id+"F4.opShell","OFFSET_FACE",FACE,{"disambiguationData":[OSD([sQuery(id+"F2.wireOp",EDGE,"E17")])]})],"blendedInto":[makeQuery(id+"F4.opShell","OFFSET_FACE",FACE,{"disambiguationData":[OSD([sQuery(id+"F2.wireOp",EDGE,"E17")])]})]});}
            var Q4;
            Q4=makeQuery(id+"F4.opShell","OFFSET_EDGE",EDGE,{"disambiguationData":[OSD([sQuery(id+"F2.wireOp",EDGE,"E16"),sQuery(id+"F2.wireOp",EDGE,"E17")])]});
            var Q5;
            {var subQ0=sQuery(id+"F2.wireOp",EDGE,"E15");Q5=makeQuery(id+"F4.opShell","OFFSET_EDGE",EDGE,{"disambiguationData":[OSD([subQ0]),TDD([makeQuery(id+"F3.opExtrude","CAP_EDGE",EDGE,{"disambiguationData":[OSD([subQ0])],"isStart":true})])]});}
            var Q6;
            Q6=makeQuery(id+"F12.opFillet","BLEND_EDGE",EDGE,{"blendedFrom":[makeQuery(id+"F3.opExtrude","CAP_EDGE",EDGE,{"disambiguationData":[OSD([sQuery(id+"F2.wireOp",EDGE,"E16")])],"isStart":true}),makeQuery(id+"F4.opShell","OFFSET_FACE",FACE,{"disambiguationData":[OSD([sQuery(id+"F2.wireOp",EDGE,"E15")])]})],"blendedInto":[makeQuery(id+"F4.opShell","OFFSET_FACE",FACE,{"disambiguationData":[OSD([sQuery(id+"F2.wireOp",EDGE,"E15")])]})]});
            var Q7;
            Q7=makeQuery(id+"F4.opShell","OFFSET_EDGE",EDGE,{"disambiguationData":[OSD([sQuery(id+"F2.wireOp",EDGE,"E15"),sQuery(id+"F2.wireOp",EDGE,"E16")])]});
            var Q8;
            Q8=makeQuery(id+"F12.opFillet","BLEND_EDGE",EDGE,{"blendedFrom":[makeQuery(id+"F3.opExtrude","CAP_EDGE",EDGE,{"disambiguationData":[OSD([sQuery(id+"F2.wireOp",EDGE,"E16")])],"isStart":false}),makeQuery(id+"F4.opShell","OFFSET_FACE",FACE,{"disambiguationData":[OSD([sQuery(id+"F2.wireOp",EDGE,"E15")])]})],"blendedInto":[makeQuery(id+"F4.opShell","OFFSET_FACE",FACE,{"disambiguationData":[OSD([sQuery(id+"F2.wireOp",EDGE,"E15")])]})]});
            var Q9;
            {var subQ0=sQuery(id+"F2.wireOp",EDGE,"E16");Q9=makeQuery(id+"F12.opFillet","BLEND_EDGE",EDGE,{"blendedFrom":[makeQuery(id+"F4.opShell","OFFSET_EDGE",EDGE,{"disambiguationData":[OSD([subQ0]),TDD([makeQuery(id+"F3.opExtrude","CAP_EDGE",EDGE,{"disambiguationData":[OSD([subQ0])],"isStart":false})])]}),makeQuery(id+"F4.opShell","OFFSET_FACE",FACE,{"disambiguationData":[OSD([sQuery(id+"F2.wireOp",EDGE,"E17")])]})],"blendedInto":[makeQuery(id+"F4.opShell","OFFSET_FACE",FACE,{"disambiguationData":[OSD([sQuery(id+"F2.wireOp",EDGE,"E17")])]})]});}
            var Q10;
            {var subQ0=sQuery(id+"F2.wireOp",EDGE,"E17");Q10=makeQuery(id+"F4.opShell","OFFSET_EDGE",EDGE,{"disambiguationData":[OSD([subQ0]),TDD([makeQuery(id+"F3.opExtrude","CAP_EDGE",EDGE,{"disambiguationData":[OSD([subQ0])],"isStart":false})])]});}
            var Q11;
            {var subQ0=sQuery(id+"F2.wireOp",EDGE,"E15");Q11=makeQuery(id+"F4.opShell","OFFSET_EDGE",EDGE,{"disambiguationData":[OSD([subQ0]),TDD([makeQuery(id+"F3.opExtrude","CAP_EDGE",EDGE,{"disambiguationData":[OSD([subQ0])],"isStart":false})])]});}
            var Q12;
            {var subQ0=sQuery(id+"F2.wireOp",EDGE,"E14");var subQ6=makeQuery(id+"F4.opShell","OFFSET_EDGE",EDGE,{"disambiguationData":[OSD([subQ0]),TDD([makeQuery(id+"F3.opExtrude","CAP_EDGE",EDGE,{"disambiguationData":[OSD([subQ0])],"isStart":false})])]});Q12=makeQuery(id+"F8.boolean.opBoolean","MERGE",EDGE,{"derivedFrom":[makeQuery(id+"F5.opBoolean","SPLIT",EDGE,{"disambiguationData":[TD([makeQuery(id+"F1.opExtrude","SWEPT_FACE",FACE,{"disambiguationData":[OSD([sQuery(id+"F0.wireOp",EDGE,"E0.top")])]})])],"derivedFrom":subQ6}),makeQuery(id+"F5.opBoolean","SPLIT",EDGE,{"disambiguationData":[TD([makeQuery(id+"F1.opExtrude","SWEPT_FACE",FACE,{"disambiguationData":[OSD([sQuery(id+"F0.wireOp",EDGE,"E2.trimOffspring")])]})])],"derivedFrom":subQ6})]});}
            var Q13;
            {var subQ0=sQuery(id+"F2.wireOp",EDGE,"E17");var subQ1=sQuery(id+"F2.wireOp",EDGE,"E14");Q13=makeQuery(id+"F6.opFillet","BLEND_EDGE",EDGE,{"blendedFrom":[makeQuery(id+"F4.opShell","OFFSET_EDGE",EDGE,{"disambiguationData":[OSD([subQ1,subQ0])]}),makeQuery(id+"F5.opBoolean","MERGE",FACE,{"derivedFrom":[makeQuery(id+"F1.opExtrude","SWEPT_FACE",FACE,{"disambiguationData":[OSD([sQuery(id+"F0.wireOp",EDGE,"E0.right")])]}),makeQuery(id+"F3.opExtrude","CAP_FACE",FACE,{"disambiguationData":[OSD([subQ1,sQuery(id+"F2.wireOp",EDGE,"E15"),sQuery(id+"F2.wireOp",EDGE,"E16"),subQ0])],"isStart":false})]})],"blendedInto":[makeQuery(id+"F5.opBoolean","MERGE",FACE,{"derivedFrom":[makeQuery(id+"F1.opExtrude","SWEPT_FACE",FACE,{"disambiguationData":[OSD([sQuery(id+"F0.wireOp",EDGE,"E0.right")])]}),makeQuery(id+"F3.opExtrude","CAP_FACE",FACE,{"disambiguationData":[OSD([subQ1,sQuery(id+"F2.wireOp",EDGE,"E15"),sQuery(id+"F2.wireOp",EDGE,"E16"),subQ0])],"isStart":false})]})]});}
            fillet(context, id + "F17", {"entities" : qUnion([Q0, Q1, Q2, Q3, Q4, Q5, Q6, Q7, Q8, Q9, Q10, Q11, Q12, Q13]), "radius" : 0.2 * mm, "tangentPropagation" : true, "allowEdgeOverflow" : false});
        }
        {
            var Q0;
            {var subQ6=sQuery(id+"F0.wireOp",EDGE,"E0.top");var subQ7=sQuery(id+"F0.wireOp",EDGE,"E0.bottom");var subQ11=sQuery(id+"F2.wireOp",EDGE,"E14");var subQ15=makeQuery(id+"F4.opShell","OFFSET_FACE",FACE,{"disambiguationData":[OSD([subQ11])]});Q0=makeQuery(id+"F8.boolean.opBoolean","MERGE",FACE,{"derivedFrom":[makeQuery(id+"F5.opBoolean","SPLIT",FACE,{"disambiguationData":[TD([makeQuery(id+"F1.opExtrude","SWEPT_FACE",FACE,{"disambiguationData":[OSD([subQ6])]})])],"derivedFrom":subQ15}),makeQuery(id+"F5.opBoolean","SPLIT",FACE,{"disambiguationData":[TD([makeQuery(id+"F1.opExtrude","SWEPT_FACE",FACE,{"disambiguationData":[OSD([subQ7])]})])],"derivedFrom":subQ15}),makeQuery(id+"F8.opExtrude","SWEPT_FACE",FACE,{"disambiguationData":[OSD([sQuery(id+"F7.wireOp",EDGE,"E19")])]})]});}
            fillet(context, id + "F18", {"entities" : qUnion([Q0]), "radius" : 350.43 * mm, "tangentPropagation" : true, "allowEdgeOverflow" : false});
        }
        {
            var Q0;
            Q0=makeQuery(id+"F13.opFillet","BLEND_FACE",FACE,{"disambiguationData":[OSD([sQuery(id+"F2.wireOp",EDGE,"E14"),sQuery(id+"F2.wireOp",EDGE,"E17")])]});
            fillet(context, id + "F19", {"entities" : qUnion([Q0]), "radius" : 3 * mm, "tangentPropagation" : true, "allowEdgeOverflow" : false});
        }
    });
